# Revit family: HL_Душевой трап_HL540I
name_source: partatom
category: Instalační zařizovací předměty
revit_build: Autodesk Revit 2016 (Build: 20151007_0715(x64)
units: mm (PartAtom-declared; Revit-internal decimal feet)

## family parameters
Bod výpočtu místnosti = Ano
Kóta kulaté spojky = Použít průměr
Nadpis OmniClass = Deck Waste Water Drains
Ořezat dutým tvarem při načtení = Ne
Sdílené = Ano
Typ součásti = Normální
Vždy vertikální = Ano
Založené na pracovní rovině = Ne
Číslo OmniClass = 23.70.50.21.24.14

## types (1)
- HL540I
    EAN = 9003076039098
    Klíčová poznámka = HL540I
    Komentáře k typům = HL540i Душевой трап "PRIMUS-DRAIN", в комплект входит дизайн-решётка HL0540I - с вкладышем для керамической плитки, "СУХОЙ" сифон, гидроизоляционный комплект для жидкой гидроизоляции, монтажные уголки для регулировки по высоте, монтажная заглушка и надставной элемент с подрамником.
    Model = HL540I
    Popis = Трапы для внутренних помещений
    Připojení CW = Ne
    Připojení HW = Ne
    Připojení odpadu = Ano
    Připojení ventilace = Ne
    URL = http://www.hutterer-lechner.com
    Výrobce = HL Hutterer & Lechner GmbH
    ВЕС = 1,89 [kg]
    ВЫСОТА МОНТАЖА = 80-200mm (88-280mm)
    МАКСИМАЛЬНАЯ НАГРУЗКА КЛАССА = K3 - 300 kg
    МАТЕРИАЛ = PP/Edelstahl
    НАСАДКА = 138x138mm/74x74mm / V4A
    НОМИНАЛЬНЫЙ ДИАМЕТР = 50 mm
    ПРОИЗВОДИТЕЛЬНОСТЬ = 0,60l/s
    ПРОПУСКНАЯ СПОСОБНОСТЬ = 0.6 L/s
    РАЗМЕР = DN50
    РЕШЁТКА = 8-30mm / 145x145mm / PP-V4A

## geometry (parser evidence)
native form markers: Sweep x12
no freeform markers — native parametric forms only
